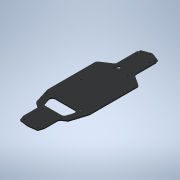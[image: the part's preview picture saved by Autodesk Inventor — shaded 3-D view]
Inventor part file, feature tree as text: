
AUTODESK INVENTOR PART (.ipt)
format: ipt  version: 2020 (Build 240168000, 168)  size: 291,328 bytes
history: native  units: mm (DEFAULTED — no unit token found)
features: hole x4, fillet x3, other x2, extrude x2, sketch x1, mirror x1
ambient origin geometry x8: Origin, YZ Plane, XZ Plane, XY Plane, X Axis, Y Axis, Z Axis, Center Point
bodies: Solid1 (feature_tree)
feature tree (13):
  sketch  "Sketch1"  dims[d1=26.0mm d2=60.0mm d3=58.0mm d4=28.75mm d6=24.0mm d9=44.0mm d13=3.0mm d14=0.0mm d15=15.0mm d16=6.0mm d19=47.5mm d20=256.5mm d21=75.0mm d22=55.0mm d23=31.5mm d24=81.0mm d25=215.0mm d26=260.0mm d27=270.0mm d28=310.0mm d29=324.0mm d30=327.0mm d31=8.0mm d32=2.0mm d43=2.0mm d99=2.0mm d100=0.0mm d101=8.0mm d110=6.0mm d190=9.0mm d191=3.0mm d192=4.0mm d193=7.5mm d195=13.0mm d196=64.0mm d197=23.0mm d198=145.0mm d199=73.0mm d213=-3.0mm d216=3.4mm d217=6.0mm d218=6.3mm d219=2.0mm d220=90.0deg d221=8.0mm d222=20.594885mm d223=3.0mm d224=6.0mm d225=6.0mm d226=2.0mm d227=90.0deg d228=8.0mm d229=20.594885mm d230=8.0mm d231=6.0mm d232=6.0mm d233=2.0mm d234=90.0deg d235=8.0mm d236=20.594885mm d242=1.0mm d243=7.0mm d244=7.0mm d245=39.0mm]
  other  "Bottom"
  hole  "Hole_Centres"  [1 undecoded]
  extrude  "Extrusion1"  Depth=8.0mm
  fillet  "Fillet1"  Radius=28.75mm
  fillet  "Fillet2"  Radius=24.0mm
  other  "5mm Inside"
  extrude  "Extrusion10"  Depth=8.0mm
  fillet  "Fillet9"  Radius=3.0mm
  hole  "Hole2"  [1 undecoded]
  hole  "Hole4"  [1 undecoded]
  mirror  "Mirror6"
  hole  "Hole3"  [1 undecoded]
note: 4 required parameter values undecoded (feature->parameter linkage not recoverable at this tier; creation-order binding heuristic only, values carry confidence <= 0.55)
